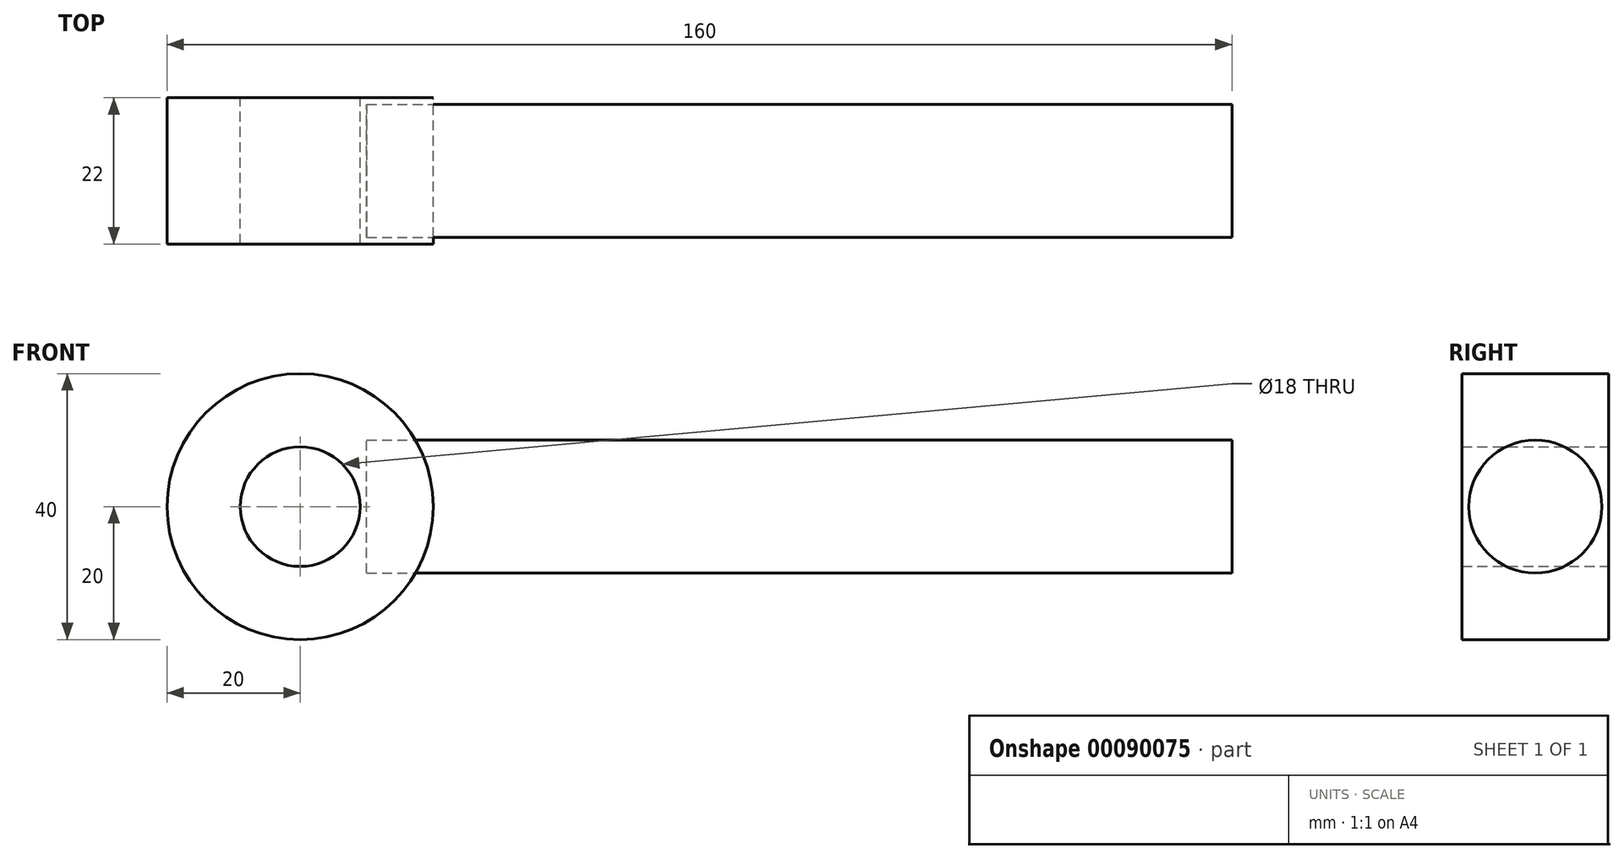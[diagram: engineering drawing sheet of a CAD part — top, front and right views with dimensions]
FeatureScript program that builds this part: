
annotation { "Feature Type Name" : "Feature", "Feature Type Description" : "" }
export const myFeature = defineFeature(function(context is Context, id is Id, definition is map)
    precondition{}
    {
        {
            var Q0;
            Q0=qCreatedBy(makeId("Front.planeOp"),FACE);
            var sketch = newSketch(context, id + "F0", { "sketchPlane" : qUnion([Q0])});
            skCircle(sketch, "E0", {"center": v(0, 0) * mm, "radius": 9 * mm});
            skCircle(sketch, "E1", {"center": v(0, 0) * mm, "radius": 20 * mm});
            skLineSegment(sketch, "E2", {"start": v(0, 0) * mm, "end": v(140, 0) * mm, "construction": true});
            skSolve(sketch);
        }
        {
            var Q0;
            Q0=makeQuery(id+"F0.imprint","IMPRINT",FACE,{"disambiguationData":[TD([[makeQuery(id+"F0.imprint","IMPRINT",EDGE,{"derivedFrom":sQuery(id+"F0.wireOp",EDGE,"E0")}),-1.0]])]});
            extrude(context, id + "F1", {"entities" : qUnion([Q0]), "depth" : 22 * mm});
        }
        {
            var Q0;
            Q0=qCreatedBy(makeId("Right.planeOp"),FACE);
            cPlane(context, id + "F2", {"entities" : qUnion([Q0]), "cplaneType" : CPlaneType.OFFSET, "offset" : 140 * mm, "width" : 150 * mm, "height" : 150 * mm});
        }
        {
            var Q0;
            Q0=qCreatedBy(id+"F2.planeOp",FACE);
            var sketch = newSketch(context, id + "F3", { "sketchPlane" : qUnion([Q0])});
            skCircle(sketch, "E3", {"center": v(-11, 0) * mm, "radius": 10 * mm});
            skLineSegment(sketch, "E4", {"start": v(-11, 0) * mm, "end": v(0, 0) * mm, "construction": true});
            skSolve(sketch);
        }
        {
            var Q0;
            Q0=makeQuery(id+"F3.imprint","IMPRINT",FACE,{"disambiguationData":[TD([[makeQuery(id+"F3.imprint","IMPRINT",EDGE,{"derivedFrom":sQuery(id+"F3.wireOp",EDGE,"E3")}),1.0]])]});
            extrude(context, id + "F4", {"entities" : qUnion([Q0]), "oppositeDirection" : true, "depth" : 130 * mm});
        }
    });
